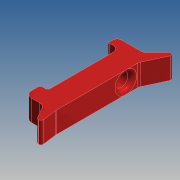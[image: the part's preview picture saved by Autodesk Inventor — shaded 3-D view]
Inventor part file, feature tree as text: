
AUTODESK INVENTOR PART (.ipt)
format: ipt  version: 2019 (Build 230136000, 136)  size: 317,440 bytes
history: native  units: mm
features: fillet x10, extrude x1, hole x1, sketch x1
ambient origin geometry x8: Origin, YZ Plane, XZ Plane, XY Plane, X Axis, Y Axis, Z Axis, Center Point
bodies: Solid1 (feature_tree)
feature tree (13):
  extrude  "Extrusion1"  Depth=2.0mm
  fillet  "Fillet1"  Radius=20.0mm
  fillet  "Fillet2"  Radius=22.0mm
  fillet  "Fillet3"  Radius=30.0mm
  fillet  "Fillet4"  Radius=4.1mm
  fillet  "Fillet5"  Radius=3.0mm
  hole  "Hole1"  [1 undecoded]
  fillet  "Fillet6"  Radius=6.0mm
  fillet  "Fillet8"  Radius=9.0mm
  fillet  "Fillet9"  [1 undecoded]
  fillet  "Fillet10"  Radius=16.0mm
  fillet  "Fillet11"  Radius=7.0mm
  sketch  "Sketch2"  dims[d1=3.0mm d2=5.0mm d3=14.0mm d4=20.0mm d5=22.0mm d6=30.0mm d7=4.1mm d8=3.0mm d9=25.0mm d10=6.0mm d11=9.0mm d12=0.0mm d13=16.0mm d14=7.0mm d15=3.5mm d16=120.0deg d17=1.308997mm d19=5.0mm d20=5.0mm d21=1.0mm d22=1.0mm d23=1.0mm d24=9.8mm d25=0.0mm d26=0.5mm d27=1.0mm d28=3.0mm d29=2.0mm d30=1.0mm d32=6.0mm d33=6.0mm d34=4.0mm d35=2.0mm d36=90.0deg d37=8.0mm d38=20.594885mm d39=2.0mm d40=45.0deg d41=3.0mm d42=10.0mm d43=5.0mm d44=12.0mm d46=1.5mm d47=1.0mm d48=2.0mm d49=1.0mm d50=2.0mm]
note: 2 required parameter values undecoded (feature->parameter linkage not recoverable at this tier; creation-order binding heuristic only, values carry confidence <= 0.55)
